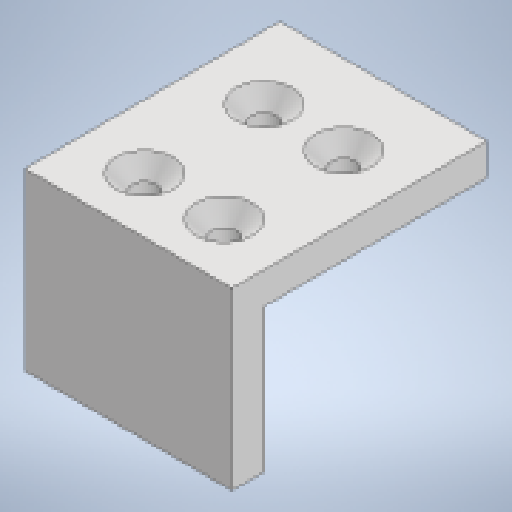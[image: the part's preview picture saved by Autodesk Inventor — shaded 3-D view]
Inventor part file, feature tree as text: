
AUTODESK INVENTOR PART (.ipt)
format: ipt  version: 2024.1 (Build 281209000, 209)  size: 237,056 bytes
history: native  units: in
note: dims shown in document units (in); Inventor stores cm internally (conversion verified against a paired STEP export)
features: sketch x4, extrude x3, chamfer x1
ambient origin geometry x8: Origin, YZ Plane, XZ Plane, XY Plane, X Axis, Y Axis, Z Axis, Center Point
bodies: Solid1 (feature_tree)
feature tree (8):
  extrude  "Extrusion1"  Depth=1.0236in
  extrude  "Extrusion2"  Depth=0.1575in
  sketch  "Sketch3"  dims[d5=0.122in d6=0.122in]
  extrude  "Extrusion3"  Depth=0.122in
  chamfer  "Chamfer1"  Distance=0.3937in
  sketch  "Sketch1"  dims[d0=1.0236in d1=1.1811in]
  sketch  "Sketch2"  dims[d2=0.1575in d3=0.0in d4=0.122in]
  sketch  "Sketch4"  dims[d7=0.122in d8=0.3937in d9=0.3937in d10=0.5906in d11=0.5906in d12=0.1969in d13=0.1969in d14=0.315in d15=0.315in d16=0.0in d17=0.0in d18=0.0787in d19=0.1575in d20=0.8661in d21=0.3937in d22=0.0in d23=0.0787in d24=0.0787in d25=45.0deg]
